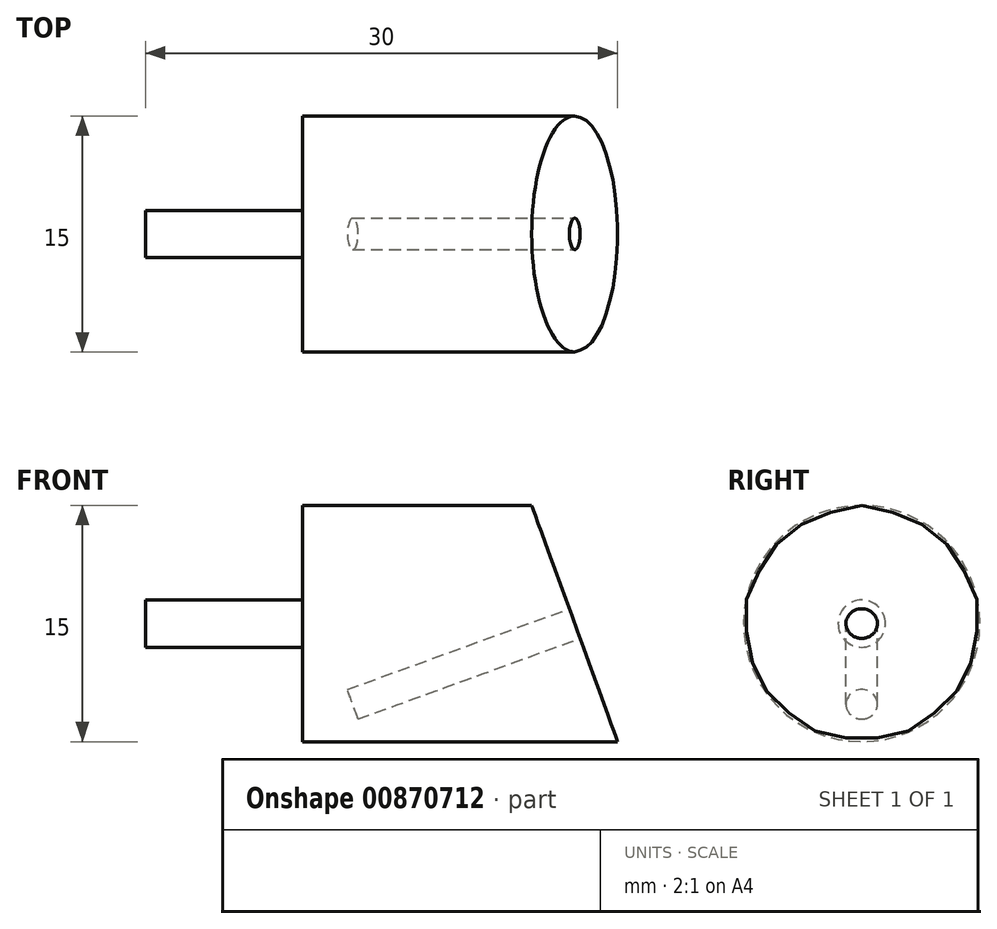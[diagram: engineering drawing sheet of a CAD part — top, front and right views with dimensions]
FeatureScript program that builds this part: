
annotation { "Feature Type Name" : "Feature", "Feature Type Description" : "" }
export const myFeature = defineFeature(function(context is Context, id is Id, definition is map)
    precondition{}
    {
        {
            var Q0;
            Q0=qCreatedBy(makeId("Front.planeOp"),FACE);
            var sketch = newSketch(context, id + "F0", { "sketchPlane" : qUnion([Q0])});
            skLineSegment(sketch, "E0", {"start": v(-40.7, 0) * mm, "end": v(58.25, 0) * mm, "construction": true});
            skLineSegment(sketch, "E1.bottom", {"start": v(10, 7.5) * mm, "end": v(30, 7.5) * mm});
            skLineSegment(sketch, "E1.top", {"start": v(0, 0) * mm, "end": v(30, 0) * mm});
            skLineSegment(sketch, "E1.left", {"start": v(0, 1.5) * mm, "end": v(0, 0) * mm});
            skLineSegment(sketch, "E1.right", {"start": v(30, 7.5) * mm, "end": v(30, 0) * mm});
            skLineSegment(sketch, "E2", {"start": v(10, 7.5) * mm, "end": v(10, 1.5) * mm});
            skLineSegment(sketch, "E3", {"start": v(10, 1.5) * mm, "end": v(0, 1.5) * mm});
            skPoint(sketch, "E4.orphan", {"position": v(0, 7.5) * mm});
            skSolve(sketch);
        }
        {
            var Q0;
            Q0=makeQuery(id+"F0.imprint","IMPRINT",FACE,{"disambiguationData":[TD([[makeQuery(id+"F0.imprint","IMPRINT",EDGE,{"derivedFrom":sQuery(id+"F0.wireOp",EDGE,"E1.bottom")}),-1.0]])]});
            var Q1;
            {var subQ2=sQuery(id+"F0.wireOp",EDGE,"E1.top");Q1=makeQuery(id+"F0.imprint","IMPRINT",FACE,{"disambiguationData":[TD([[makeQuery(id+"F0.imprint","IMPRINT",EDGE,{"derivedFrom":subQ2}),1.0]])]});}
            var Q2;
            Q2=sQuery(id+"F0.wireOp",EDGE,"E0");
            revolve(context, id + "F1", {"surfaceOperationType" : NewSurfaceOperationType.NEW, "entities" : qUnion([Q0, Q1]), "axis" : qUnion([Q2]), "revolveType" : RevolveType.FULL});
        }
        {
            var Q0;
            Q0=qCreatedBy(makeId("Front.planeOp"),FACE);
            var sketch = newSketch(context, id + "F2", { "sketchPlane" : qUnion([Q0])});
            skLineSegment(sketch, "E5", {"start": v(30, -7.5) * mm, "end": v(24.54, 7.5) * mm});
            skLineSegment(sketch, "E6", {"start": v(24.54, 7.5) * mm, "end": v(30, 7.5) * mm});
            skLineSegment(sketch, "E7", {"start": v(30, 7.5) * mm, "end": v(30, -7.5) * mm});
            skSolve(sketch);
        }
        {
            var Q0;
            Q0 = qSketchRegion(id + "F2", true);
            extrude(context, id + "F3", {"entities" : qUnion([Q0]), "operationType" : NewBodyOperationType.REMOVE, "endBound" : BoundingType.THROUGH_ALL, "oppositeDirection" : true, "depth" : 25 * mm, "offsetDistance" : 25 * mm, "hasSecondDirection" : true, "secondDirectionBound" : SecondDirectionBoundingType.THROUGH_ALL, "secondDirectionOppositeDirection" : false, "secondDirectionDepth" : 25 * mm});
        }
        {
            var Q0;
            Q0=makeQuery(id+"F3.boolean.opBoolean","COPY",FACE,{"derivedFrom":makeQuery(id+"F3.opExtrude","SWEPT_FACE",FACE,{"disambiguationData":[OSD([sQuery(id+"F2.wireOp",EDGE,"E5")])]})});
            var sketch = newSketch(context, id + "F4", { "sketchPlane" : qUnion([Q0])});
            skCircle(sketch, "E8", {"center": v(0, -9.33) * mm, "radius": 1 * mm});
            skSolve(sketch);
        }
        {
            var Q0;
            Q0=makeQuery(id+"F4.imprint","IMPRINT",FACE,{"disambiguationData":[TD([[makeQuery(id+"F4.imprint","IMPRINT",EDGE,{"derivedFrom":sQuery(id+"F4.wireOp",EDGE,"E8")}),1.0]])]});
            extrude(context, id + "F5", {"entities" : qUnion([Q0]), "operationType" : NewBodyOperationType.REMOVE, "oppositeDirection" : true, "depth" : 15 * mm, "offsetDistance" : 25 * mm});
        }
    });
